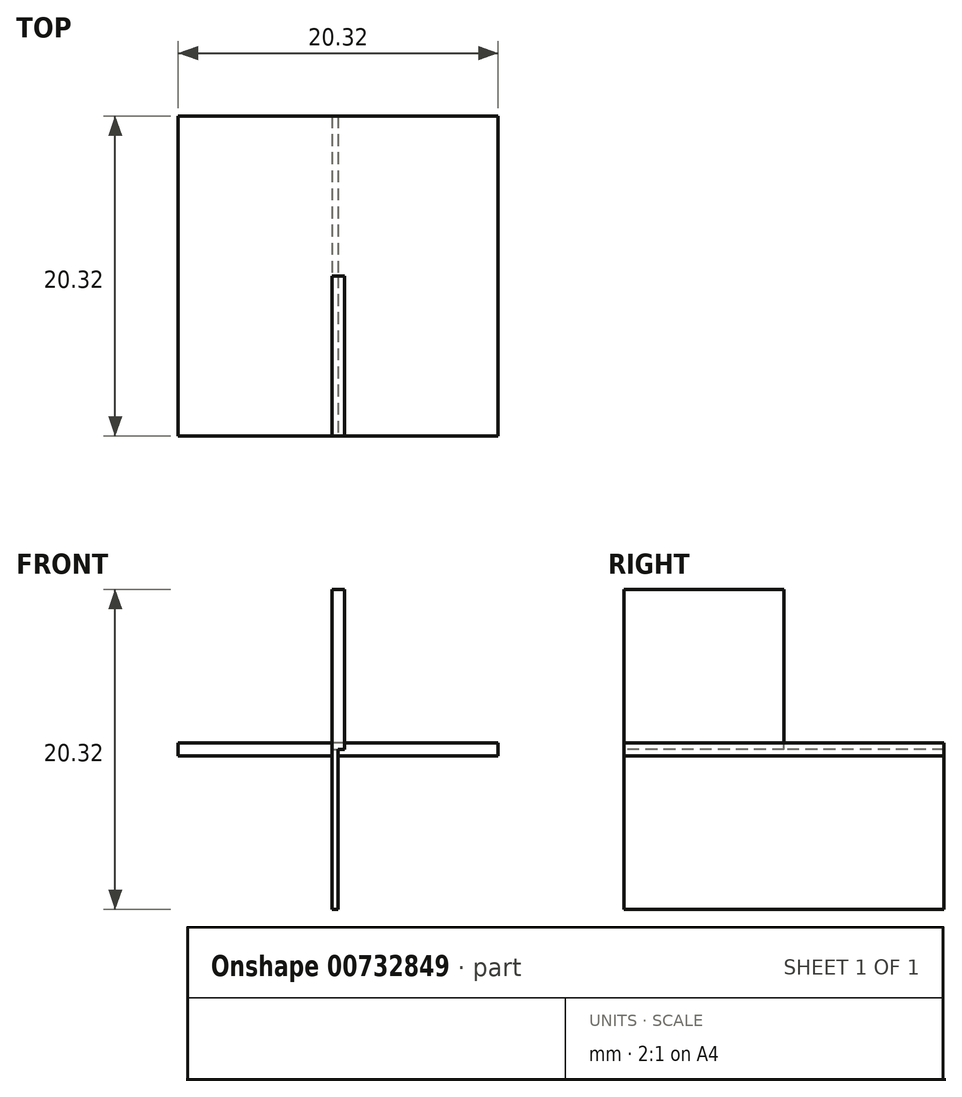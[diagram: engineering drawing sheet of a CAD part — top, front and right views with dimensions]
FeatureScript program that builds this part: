
annotation { "Feature Type Name" : "Feature", "Feature Type Description" : "" }
export const myFeature = defineFeature(function(context is Context, id is Id, definition is map)
    precondition{}
    {
        {
            assignVariable(context, id + "F0", {"name" : "l", "anyValue" : .8});
        }
        {
            var Q0;
            Q0=qCreatedBy(makeId("Right.planeOp"),FACE);
            var sketch = newSketch(context, id + "F1", { "sketchPlane" : qUnion([Q0])});
            skLineSegment(sketch, "E0", {"start": v(0, 0) * mm, "end": v(0, 10.16) * mm});
            skLineSegment(sketch, "E1", {"start": v(0, 10.16) * mm, "end": v(-10.16, 10.16) * mm});
            skLineSegment(sketch, "E2", {"start": v(-10.16, 10.16) * mm, "end": v(-10.16, -10.16) * mm});
            skLineSegment(sketch, "E3", {"start": v(-10.16, -10.16) * mm, "end": v(10.16, -10.16) * mm});
            skLineSegment(sketch, "E4", {"start": v(10.16, -10.16) * mm, "end": v(10.16, 0) * mm});
            skLineSegment(sketch, "E5", {"start": v(10.16, 0) * mm, "end": v(0, 0) * mm});
            skSolve(sketch);
        }
        {
            var Q0;
            Q0=makeQuery(id+"F1.imprint","IMPRINT",FACE,{"disambiguationData":[TD([[makeQuery(id+"F1.imprint","IMPRINT",EDGE,{"derivedFrom":sQuery(id+"F1.wireOp",EDGE,"E0")}),1.0]])]});
            extrude(context, id + "F2", {"entities" : qUnion([Q0]), "oppositeDirection" : true, "depth" : (getVariable(context, 'l') / 2) * mm, "offsetDistance" : 25.4 * mm});
        }
        {
            var Q0;
            Q0=makeQuery(id+"F2.opExtrude","CAP_FACE",FACE,{"disambiguationData":[OSD([sQuery(id+"F1.wireOp",EDGE,"E0"),sQuery(id+"F1.wireOp",EDGE,"E1"),sQuery(id+"F1.wireOp",EDGE,"E2"),sQuery(id+"F1.wireOp",EDGE,"E3"),sQuery(id+"F1.wireOp",EDGE,"E4"),sQuery(id+"F1.wireOp",EDGE,"E5")])],"isStart":true});
            var sketch = newSketch(context, id + "F3", { "sketchPlane" : qUnion([Q0])});
            skLineSegment(sketch, "E6.bottom", {"start": v(0, 0) * mm, "end": v(-10.16, 0) * mm});
            skLineSegment(sketch, "E6.top", {"start": v(0, 10.16) * mm, "end": v(-10.16, 10.16) * mm});
            skLineSegment(sketch, "E6.left", {"start": v(0, 0) * mm, "end": v(0, 10.16) * mm});
            skLineSegment(sketch, "E6.right", {"start": v(-10.16, 0) * mm, "end": v(-10.16, 10.16) * mm});
            skSolve(sketch);
        }
        {
            var Q0;
            Q0=makeQuery(id+"F3.imprint","IMPRINT",FACE,{"disambiguationData":[TD([[makeQuery(id+"F3.imprint","IMPRINT",EDGE,{"derivedFrom":sQuery(id+"F3.wireOp",EDGE,"E6.bottom")}),-1.0]])]});
            extrude(context, id + "F4", {"entities" : qUnion([Q0]), "operationType" : NewBodyOperationType.ADD, "depth" : (getVariable(context, 'l') / 2) * mm, "offsetDistance" : 25.4 * mm});
        }
        {
            var Q0;
            Q0=qCreatedBy(makeId("Top.planeOp"),FACE);
            var sketch = newSketch(context, id + "F5", { "sketchPlane" : qUnion([Q0])});
            skLineSegment(sketch, "E7.bottom", {"start": v(10.16, 10.16) * mm, "end": v(-10.16, 10.16) * mm});
            skLineSegment(sketch, "E7.top", {"start": v(10.16, -10.16) * mm, "end": v(-10.16, -10.16) * mm});
            skLineSegment(sketch, "E7.left", {"start": v(10.16, 10.16) * mm, "end": v(10.16, -10.16) * mm});
            skLineSegment(sketch, "E7.right", {"start": v(-10.16, 10.16) * mm, "end": v(-10.16, -10.16) * mm});
            skPoint(sketch, "E7.middle", {"position": v(0, 0) * mm});
            skSolve(sketch);
        }
        {
            var Q0;
            Q0=makeQuery(id+"F5.imprint","IMPRINT",FACE,{"disambiguationData":[TD([[makeQuery(id+"F5.imprint","IMPRINT",EDGE,{"derivedFrom":sQuery(id+"F5.wireOp",EDGE,"E7.bottom")}),1.0]])]});
            extrude(context, id + "F6", {"entities" : qUnion([Q0]), "depth" : (getVariable(context, 'l') / 2) * mm, "offsetDistance" : 25.4 * mm, "hasSecondDirection" : true, "secondDirectionOppositeDirection" : true, "secondDirectionDepth" : (getVariable(context, 'l') / 2) * mm});
        }
        {
            var Q0;
            Q0=makeQuery(id+"F2.opExtrude","SWEPT_BODY",BODY,{"disambiguationData":[OSD([sQuery(id+"F1.wireOp",EDGE,"E0"),sQuery(id+"F1.wireOp",EDGE,"E1"),sQuery(id+"F1.wireOp",EDGE,"E2"),sQuery(id+"F1.wireOp",EDGE,"E3"),sQuery(id+"F1.wireOp",EDGE,"E4"),sQuery(id+"F1.wireOp",EDGE,"E5")])]});
            var Q1;
            Q1=makeQuery(id+"F6.opExtrude","SWEPT_BODY",BODY,{"disambiguationData":[OSD([sQuery(id+"F5.wireOp",EDGE,"E7.bottom"),sQuery(id+"F5.wireOp",EDGE,"E7.top"),sQuery(id+"F5.wireOp",EDGE,"E7.left"),sQuery(id+"F5.wireOp",EDGE,"E7.right")])]});
            booleanBodies(context, id + "F7", {"operationType" : BooleanOperationType.SUBTRACTION, "tools" : qUnion([Q0]), "targets" : qUnion([Q1]), "keepTools" : true});
        }
    });
